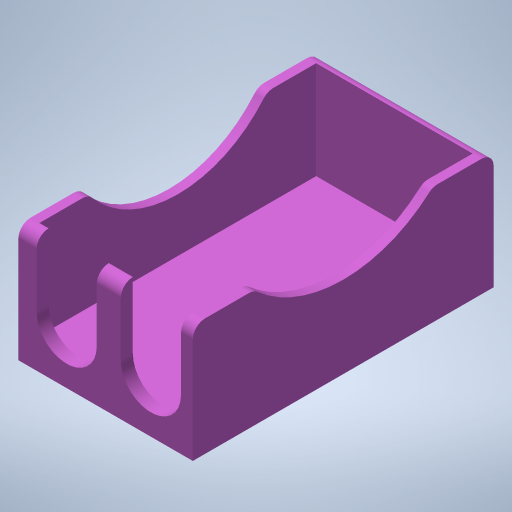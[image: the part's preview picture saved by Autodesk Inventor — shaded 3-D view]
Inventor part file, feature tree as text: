
AUTODESK INVENTOR PART (.ipt)
format: ipt  version: 2024 (Build 280153000, 153)  size: 262,144 bytes
history: native  units: mm
features: extrude x5, sketch x5, other x1, fillet x1
ambient origin geometry x8: Origin, YZ Plane, XZ Plane, XY Plane, X Axis, Y Axis, Z Axis, Center Point
bodies: Body1 (feature_tree)
feature tree (12):
  other  "Sólido1"
  extrude  "Extrusión1"  Depth=26.0mm
  extrude  "Extrusión2"  Depth=1.5mm
  extrude  "Extrusión3"  Depth=16.25mm TaperAngle=0.0deg
  extrude  "Extrusión4"  Depth=10.0mm
  extrude  "Extrusión5"  Depth=4.0mm
  fillet  "Empalme1"  Radius=11.0mm
  sketch  "Boceto1"  dims[d0=46.0mm d1=26.0mm]
  sketch  "Boceto2"  dims[d2=2.0mm d3=1.5mm]
  sketch  "Boceto3"  dims[d4=19.5mm d5=0.0mm d6=16.25mm d7=0.0mm]
  sketch  "Boceto4"  dims[d8=11.0mm d10=10.0mm]
  sketch  "Boceto5"  dims[d11=10.0mm d12=4.0mm d13=11.0mm d14=11.0mm d15=11.0mm d16=17.0mm d17=0.0mm d18=10.16mm d19=10.16mm d20=17.0mm d21=0.0mm d22=10.16mm d23=10.16mm d24=17.0mm d25=0.0mm d26=2.0mm]
